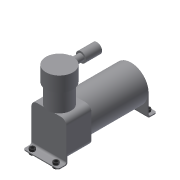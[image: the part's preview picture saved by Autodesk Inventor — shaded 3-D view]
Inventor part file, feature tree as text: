
AUTODESK INVENTOR PART (.ipt)
format: ipt  version: 2013 (Build 170138000, 138)  size: 256,512 bytes
history: native  units: in
note: dims shown in document units (in); Inventor stores cm internally (conversion verified against a paired STEP export)
features: sketch x15, extrude x13, fillet x5, hole x2, projected_geometry x1
ambient origin geometry x8: Origin, YZ Plane, XZ Plane, XY Plane, X Axis, Y Axis, Z Axis, Center Point
bodies: Solid1 (feature_tree), Solid2 (feature_tree)
feature tree (36):
  extrude  "Extrusion1"  Depth=3.38in TaperAngle=0.0deg
  extrude  "Extrusion2"  Depth=1.4138in
  extrude  "Extrusion3"  Depth=1.625in
  extrude  "Extrusion4"  Depth=0.04in
  extrude  "Extrusion5"  Depth=0.4625in TaperAngle=0.0deg
  extrude  "Extrusion6"  Depth=0.06in
  extrude  "Extrusion7"  Depth=0.06in
  extrude  "Extrusion8"  Depth=0.125in
  fillet  "Fillet1"  Radius=1.42in
  hole  "Hole1"  [1 undecoded]
  fillet  "Fillet2"  Radius=0.06in
  extrude  "Extrusion9"  Depth=0.06in
  extrude  "Extrusion10"  Depth=0.125in
  fillet  "Fillet3"  Radius=1.42in
  hole  "Hole2"  [1 undecoded]
  fillet  "Fillet4"  Radius=0.0275in
  extrude  "Extrusion11"  Depth=0.5in TaperAngle=0.0deg
  extrude  "Extrusion12"  Depth=0.313in
  extrude  "Extrusion13"  Depth=0.125in TaperAngle=0.0deg
  fillet  "Fillet5"  Radius=0.313in
  sketch  "Sketch1"  dims[d0=2.11in d1=3.38in d2=0.0in]
  sketch  "Sketch2"  dims[d3=1.5in d4=0.0in d5=1.4138in]
  sketch  "Sketch3"  dims[d7=1.145in d8=0.0in d9=1.625in]
  sketch  "Sketch4"  dims[d10=0.3in d11=0.04in]
  sketch  "Sketch5"  dims[d12=0.9in d13=0.0in d14=0.4625in d15=0.0in]
  sketch  "Sketch6"  dims[d16=0.9625in d17=0.0in d18=0.06in]
  sketch  "Sketch7"  dims[d20=0.25in d21=0.0in d22=0.06in]
  sketch  "Sketch8"  dims[d24=0.5in d25=0.0in d26=0.125in d27=1.42in]
  sketch  "Sketch9"  dims[d29=0.19in d30=0.75in d31=0.375in d32=0.25in d33=0.5635in d34=1.0in d35=0.8108in d36=0.125in d37=0.06in d38=0.0in]
  sketch  "Sketch10"  dims[d39=0.185in d42=0.06in]
  projected_geometry  "Projected Loop1"
  sketch  "Sketch11"  dims[d44=0.5in d45=0.0in d46=0.125in d47=1.42in]
  sketch  "Sketch12"  dims[d49=0.19in d50=0.75in d51=0.375in d52=0.25in d53=0.5635in d54=1.0in d55=0.8108in d56=0.125in d57=0.0275in]
  sketch  "Sketch13"  dims[d59=0.0275in d60=0.5in d61=0.0in]
  sketch  "Sketch14"  dims[d62=0.5in d63=0.0in d64=0.313in]
  sketch  "Sketch15"  dims[d65=0.313in d66=0.125in d67=0.185in d68=0.0in d69=0.0in d70=0.313in d71=0.313in d72=0.325in]
note: 2 required parameter values undecoded (feature->parameter linkage not recoverable at this tier; creation-order binding heuristic only, values carry confidence <= 0.55)
